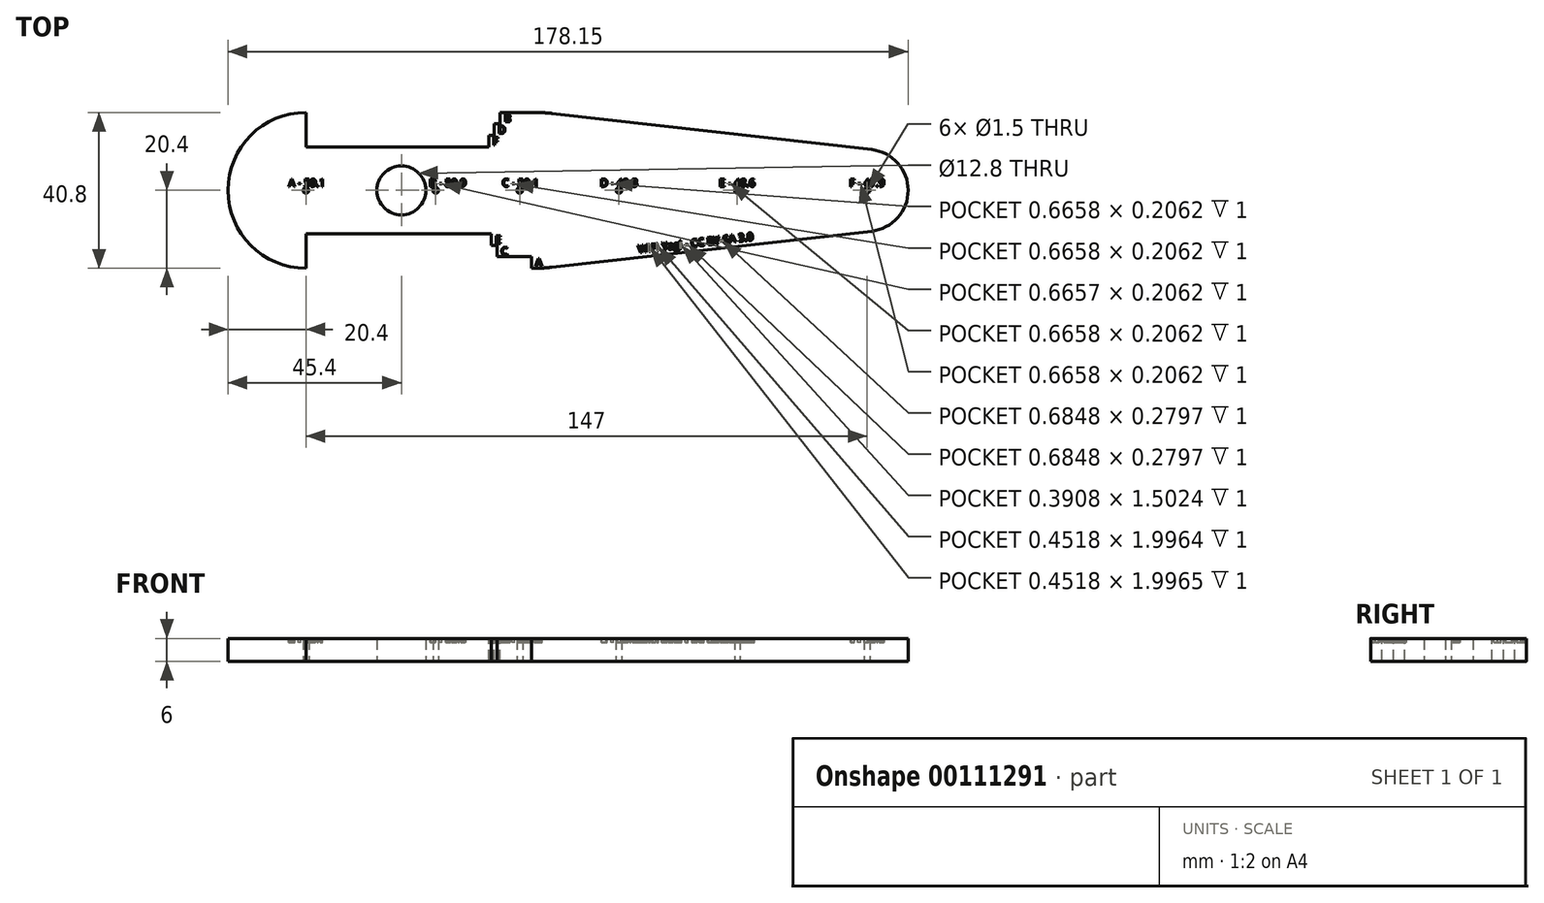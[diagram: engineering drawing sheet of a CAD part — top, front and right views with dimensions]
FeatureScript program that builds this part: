
annotation { "Feature Type Name" : "Feature", "Feature Type Description" : "" }
export const myFeature = defineFeature(function(context is Context, id is Id, definition is map)
    precondition{}
    {
        {
            var Q0;
            Q0=qCreatedBy(makeId("Top.planeOp"),FACE);
            var sketch = newSketch(context, id + "F0", { "sketchPlane" : qUnion([Q0])});
            skCircle(sketch, "E0", {"center": v(0, 0) * mm, "radius": 6.4 * mm});
            skCircle(sketch, "E1", {"center": v(9, 0) * mm, "radius": 0.75 * mm});
            skCircle(sketch, "E2", {"center": v(31, 0) * mm, "radius": 0.75 * mm});
            skCircle(sketch, "E3", {"center": v(57, 0) * mm, "radius": 0.75 * mm});
            skCircle(sketch, "E4", {"center": v(88, 0) * mm, "radius": 0.75 * mm});
            skLineSegment(sketch, "E5", {"start": v(0, 0) * mm, "end": v(9, 0) * mm, "construction": true});
            skLineSegment(sketch, "E6", {"start": v(9, 0) * mm, "end": v(31, 0) * mm, "construction": true});
            skLineSegment(sketch, "E7", {"start": v(31, 0) * mm, "end": v(57, 0) * mm, "construction": true});
            skLineSegment(sketch, "E8", {"start": v(57, 0) * mm, "end": v(88, 0) * mm, "construction": true});
            skCircle(sketch, "E9", {"center": v(-25, 0) * mm, "radius": 0.75 * mm});
            skLineSegment(sketch, "E10", {"start": v(-25, 0) * mm, "end": v(0, 0) * mm, "construction": true});
            skCircle(sketch, "E11", {"center": v(122, 0) * mm, "radius": 0.75 * mm});
            skLineSegment(sketch, "E12", {"start": v(88, 0) * mm, "end": v(122, 0) * mm, "construction": true});
            skArc(sketch, "E13", {"start": v(-25, 20.4) * mm, "mid": v(-45.4, 0) * mm, "end": v(-25, -20.4) * mm});
            skLineSegment(sketch, "E14", {"start": v(-25, 20.4) * mm, "end": v(35, 20.4) * mm});
            skLineSegment(sketch, "E15", {"start": v(39.5, 20.15) * mm, "end": v(123.2, 10.68) * mm});
            skArc(sketch, "E16", {"start": v(123.2, -10.68) * mm, "mid": v(132.75, 0) * mm, "end": v(123.2, 10.68) * mm});
            skLineSegment(sketch, "E17", {"start": v(-25, -20.4) * mm, "end": v(35, -20.4) * mm});
            skLineSegment(sketch, "E18", {"start": v(39.5, -20.15) * mm, "end": v(123.2, -10.68) * mm});
            skPoint(sketch, "E19.visualSharp", {"position": v(37.25, 20.4) * mm});
            skArc(sketch, "E19.filletArc", {"start": v(39.5, 20.15) * mm, "mid": v(37.25, 20.34) * mm, "end": v(35, 20.4) * mm});
            skPoint(sketch, "E20.visualSharp", {"position": v(37.25, -20.4) * mm});
            skArc(sketch, "E20.filletArc", {"start": v(35, -20.4) * mm, "mid": v(37.25, -20.34) * mm, "end": v(39.5, -20.15) * mm});
            skSolve(sketch);
        }
        {
            var Q0;
            Q0 = qSketchRegion(id + "F0", true);
            extrude(context, id + "F1", {"entities" : qUnion([Q0]), "depth" : 6 * mm});
        }
        {
            var Q0;
            Q0=makeQuery(id+"F1.opExtrude","CAP_FACE",FACE,{"disambiguationData":[OSD([sQuery(id+"F0.wireOp",EDGE,"E0"),sQuery(id+"F0.wireOp",EDGE,"E1"),sQuery(id+"F0.wireOp",EDGE,"E2"),sQuery(id+"F0.wireOp",EDGE,"E3"),sQuery(id+"F0.wireOp",EDGE,"E4"),sQuery(id+"F0.wireOp",EDGE,"E9"),sQuery(id+"F0.wireOp",EDGE,"E11"),sQuery(id+"F0.wireOp",EDGE,"E13"),sQuery(id+"F0.wireOp",EDGE,"E14"),sQuery(id+"F0.wireOp",EDGE,"E15"),sQuery(id+"F0.wireOp",EDGE,"E16"),sQuery(id+"F0.wireOp",EDGE,"E17"),sQuery(id+"F0.wireOp",EDGE,"E18"),sQuery(id+"F0.wireOp",EDGE,"E19.filletArc"),sQuery(id+"F0.wireOp",EDGE,"E20.filletArc")])],"isStart":false});
            var sketch = newSketch(context, id + "F2", { "sketchPlane" : qUnion([Q0])});
            skLineSegment(sketch, "E21", {"start": v(25.9, 20.4) * mm, "end": v(25.9, 17.4) * mm});
            skLineSegment(sketch, "E22", {"start": v(24.3, 17.4) * mm, "end": v(25.9, 17.4) * mm});
            skLineSegment(sketch, "E23", {"start": v(24.3, 17.4) * mm, "end": v(24.3, 14.4) * mm});
            skLineSegment(sketch, "E24", {"start": v(22.9, 14.4) * mm, "end": v(24.3, 14.4) * mm});
            skLineSegment(sketch, "E25", {"start": v(22.9, 14.4) * mm, "end": v(22.9, 11.4) * mm});
            skLineSegment(sketch, "E26", {"start": v(-25, 11.4) * mm, "end": v(22.9, 11.4) * mm});
            skLineSegment(sketch, "E27", {"start": v(-25, -20.4) * mm, "end": v(-25, -11.4) * mm});
            skLineSegment(sketch, "E28", {"start": v(23.6, -11.4) * mm, "end": v(-25, -11.4) * mm});
            skLineSegment(sketch, "E29", {"start": v(23.6, -11.4) * mm, "end": v(23.6, -14.4) * mm});
            skLineSegment(sketch, "E30", {"start": v(23.6, -14.4) * mm, "end": v(25.1, -14.4) * mm});
            skLineSegment(sketch, "E31", {"start": v(25.1, -14.4) * mm, "end": v(25.1, -17.4) * mm});
            skLineSegment(sketch, "E32", {"start": v(25.1, -17.4) * mm, "end": v(34.1, -17.4) * mm});
            skLineSegment(sketch, "E33", {"start": v(34.1, -17.4) * mm, "end": v(34.1, -20.4) * mm});
            skLineSegment(sketch, "E34", {"start": v(34.1, -20.4) * mm, "end": v(-25, -20.4) * mm});
            skLineSegment(sketch, "E35", {"start": v(25.9, 20.4) * mm, "end": v(-25, 20.4) * mm});
            skLineSegment(sketch, "E36", {"start": v(-25, 20.4) * mm, "end": v(-25, 11.4) * mm});
            skText(sketch, "E37", { "text": "A - 59.1", "fontName": "OpenSans-Regular.ttf"});
            skText(sketch, "E38", { "text": "B - 50.9", "fontName": "OpenSans-Regular.ttf"});
            skText(sketch, "E39", { "text": "C - 50.1", "fontName": "OpenSans-Regular.ttf"});
            skText(sketch, "E40", { "text": "D - 49.3", "fontName": "OpenSans-Regular.ttf"});
            skText(sketch, "E41", { "text": "E - 48.6", "fontName": "OpenSans-Regular.ttf"});
            skText(sketch, "E42", { "text": "F - 47.9", "fontName": "OpenSans-Regular.ttf"});
            skLineSegment(sketch, "E43", {"start": v(122, 0) * mm, "end": v(122, 1) * mm, "construction": true});
            skLineSegment(sketch, "E44", {"start": v(88, 1) * mm, "end": v(88, 0) * mm, "construction": true});
            skLineSegment(sketch, "E45", {"start": v(57, 1) * mm, "end": v(57, 0) * mm, "construction": true});
            skLineSegment(sketch, "E46", {"start": v(31, 0) * mm, "end": v(31, 1) * mm, "construction": true});
            skLineSegment(sketch, "E47", {"start": v(9, 0) * mm, "end": v(9, 1) * mm, "construction": true});
            skLineSegment(sketch, "E48", {"start": v(-25, 0) * mm, "end": v(-25, 1) * mm, "construction": true});
            skText(sketch, "E49", { "text": "F", "fontName": "OpenSans-Regular.ttf"});
            skText(sketch, "E50", { "text": "B", "fontName": "OpenSans-Regular.ttf"});
            skLineSegment(sketch, "E51", {"start": v(22.9, 12.9) * mm, "end": v(23.9, 12.9) * mm, "construction": true});
            skLineSegment(sketch, "E52", {"start": v(24.3, 15.9) * mm, "end": v(25.3, 15.9) * mm, "construction": true});
            skLineSegment(sketch, "E53", {"start": v(25.9, 18.9) * mm, "end": v(26.9, 18.9) * mm, "construction": true});
            skText(sketch, "E54", { "text": "D", "fontName": "OpenSans-Regular.ttf"});
            skText(sketch, "E55", { "text": "E", "fontName": "OpenSans-Regular.ttf"});
            skText(sketch, "E56", { "text": "C", "fontName": "OpenSans-Regular.ttf"});
            skText(sketch, "E57", { "text": "A", "fontName": "OpenSans-Regular.ttf"});
            skLineSegment(sketch, "E58", {"start": v(24.6, -12.9) * mm, "end": v(23.6, -12.9) * mm, "construction": true});
            skLineSegment(sketch, "E59", {"start": v(26.1, -15.9) * mm, "end": v(25.1, -15.9) * mm, "construction": true});
            skLineSegment(sketch, "E60", {"start": v(35.1, -18.9) * mm, "end": v(34.1, -18.9) * mm, "construction": true});
            const initialGuessF2  = {"E37": [-0.02958, 0.001, 1, 0, 0.002], "E38": [0.00733, 0.001, 1, 0, 0.002], "E39": [0.02642, 0.001, 1, 0, 0.002], "E40": [0.05206, 0.001, 1, 0, 0.002], "E41": [0.08328, 0.001, 1, 0, 0.002], "E42": [0.11735, 0.001, 1, 0, 0.002], "E49": [0.0239, 0.0119, 1, 0, 0.002], "E50": [0.0269, 0.0179, 1, 0, 0.002], "E54": [0.0253, 0.0149, 1, 0, 0.002], "E55": [0.0246, -0.0139, 1, 0, 0.002], "E56": [0.0261, -0.0169, 1, 0, 0.002], "E57": [0.0351, -0.0199, 1, 0, 0.002]};
            skSetInitialGuess(sketch, initialGuessF2);
            skSolve(sketch);
        }
        {
            var Q0;
            Q0 = qSketchRegion(id + "F2", true);
            extrude(context, id + "F3", {"entities" : qUnion([Q0]), "operationType" : NewBodyOperationType.REMOVE, "oppositeDirection" : true, "depth" : 1 * mm});
        }
        {
            var Q0;
            {var subQ0=sQuery(id+"F0.wireOp",EDGE,"E20.filletArc");var subQ1=sQuery(id+"F0.wireOp",EDGE,"E1");var subQ2=sQuery(id+"F0.wireOp",EDGE,"E15");var subQ3=sQuery(id+"F0.wireOp",EDGE,"E17");var subQ4=sQuery(id+"F0.wireOp",EDGE,"E2");var subQ5=sQuery(id+"F0.wireOp",EDGE,"E0");var subQ6=sQuery(id+"F0.wireOp",EDGE,"E16");var subQ7=sQuery(id+"F0.wireOp",EDGE,"E3");var subQ8=sQuery(id+"F0.wireOp",EDGE,"E9");var subQ9=sQuery(id+"F0.wireOp",EDGE,"E18");var subQ10=sQuery(id+"F0.wireOp",EDGE,"E4");var subQ11=sQuery(id+"F0.wireOp",EDGE,"E11");var subQ12=sQuery(id+"F0.wireOp",EDGE,"E13");var subQ13=sQuery(id+"F0.wireOp",EDGE,"E14");var subQ14=sQuery(id+"F0.wireOp",EDGE,"E19.filletArc");Q0=makeQuery(id+"F3.boolean.opBoolean","SPLIT",FACE,{"disambiguationData":[TD([makeQuery(id+"F1.opExtrude","SWEPT_FACE",FACE,{"disambiguationData":[OSD([subQ5])]})])],"derivedFrom":makeQuery(id+"F1.opExtrude","CAP_FACE",FACE,{"disambiguationData":[OSD([subQ5,subQ1,subQ4,subQ7,subQ10,subQ8,subQ11,subQ12,subQ13,subQ2,subQ6,subQ3,subQ9,subQ14,subQ0])],"isStart":false})});}
            var sketch = newSketch(context, id + "F4", { "sketchPlane" : qUnion([Q0])});
            skText(sketch, "E61", { "text": "WIFI Yagi - CC BY-SA 3.0", "fontName": "OpenSans-Regular.ttf"});
            const initialGuessF4  = {"E61": [0.06211, -0.01643, 0.99367, 0.11235, 0.002]};
            skSetInitialGuess(sketch, initialGuessF4);
            skSolve(sketch);
        }
        {
            var Q0;
            Q0 = qSketchRegion(id + "F4", true);
            extrude(context, id + "F5", {"entities" : qUnion([Q0]), "operationType" : NewBodyOperationType.REMOVE, "oppositeDirection" : true, "depth" : 1 * mm});
        }
        {
            var Q0;
            Q0=makeQuery(id+"F3.boolean.opBoolean","COPY",FACE,{"derivedFrom":makeQuery(id+"F3.opExtrude","CAP_FACE",FACE,{"disambiguationData":[OSD([sQuery(id+"F2.wireOp",EDGE,"E21"),sQuery(id+"F2.wireOp",EDGE,"E22"),sQuery(id+"F2.wireOp",EDGE,"E23"),sQuery(id+"F2.wireOp",EDGE,"E24"),sQuery(id+"F2.wireOp",EDGE,"E25"),sQuery(id+"F2.wireOp",EDGE,"E26"),sQuery(id+"F2.wireOp",EDGE,"E35"),sQuery(id+"F2.wireOp",EDGE,"E36")])],"isStart":false})});
            var Q1;
            Q1=makeQuery(id+"F3.boolean.opBoolean","COPY",FACE,{"derivedFrom":makeQuery(id+"F3.opExtrude","CAP_FACE",FACE,{"disambiguationData":[OSD([sQuery(id+"F2.wireOp",EDGE,"E27"),sQuery(id+"F2.wireOp",EDGE,"E28"),sQuery(id+"F2.wireOp",EDGE,"E29"),sQuery(id+"F2.wireOp",EDGE,"E30"),sQuery(id+"F2.wireOp",EDGE,"E31"),sQuery(id+"F2.wireOp",EDGE,"E32"),sQuery(id+"F2.wireOp",EDGE,"E33"),sQuery(id+"F2.wireOp",EDGE,"E34")])],"isStart":false})});
            extrude(context, id + "F6", {"entities" : qUnion([Q0, Q1]), "operationType" : NewBodyOperationType.REMOVE, "endBound" : BoundingType.THROUGH_ALL, "oppositeDirection" : true, "depth" : 25 * mm});
        }
    });
